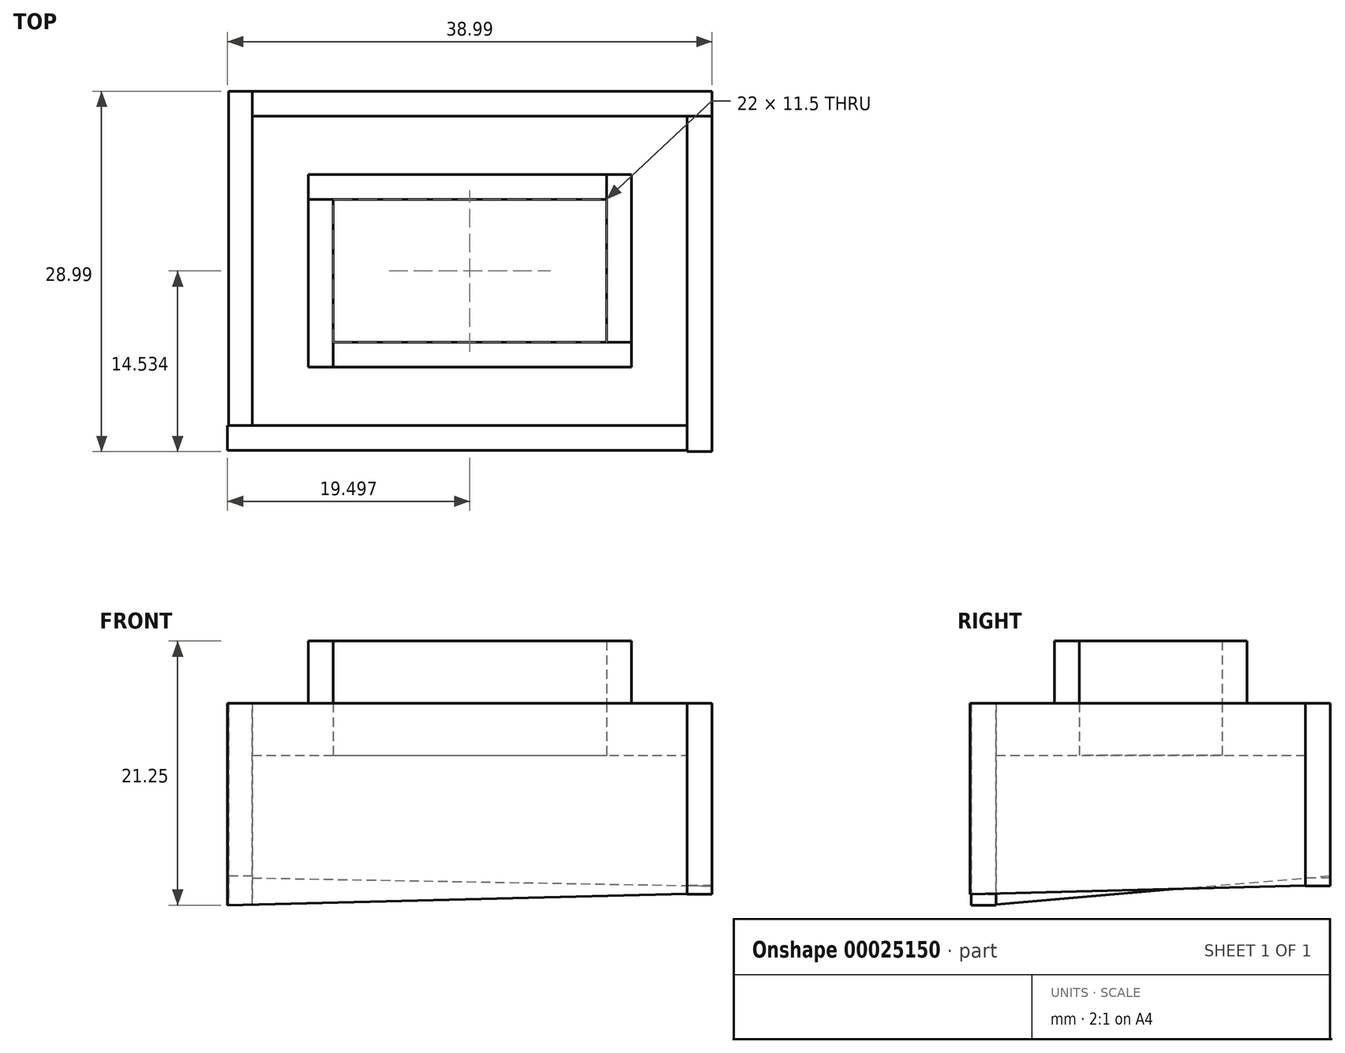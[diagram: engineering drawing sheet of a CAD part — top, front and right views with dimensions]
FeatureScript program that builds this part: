
annotation { "Feature Type Name" : "Feature", "Feature Type Description" : "" }
export const myFeature = defineFeature(function(context is Context, id is Id, definition is map)
    precondition{}
    {
        {
            var Q0;
            Q0=qCreatedBy(makeId("Top.planeOp"),FACE);
            cPlane(context, id + "F0", {"entities" : qUnion([Q0]), "cplaneType" : CPlaneType.OFFSET, "offset" : (12 + 4.2) * mm, "width" : 150 * mm, "height" : 150 * mm});
        }
        {
            var Q0;
            Q0=qCreatedBy(makeId("Right.planeOp"),FACE);
            var sketch = newSketch(context, id + "F1", { "sketchPlane" : qUnion([Q0])});
            skLineSegment(sketch, "E0", {"start": v(0, 0) * mm, "end": v(24.9, 2.14) * mm});
            skLineSegment(sketch, "E1", {"start": v(0, 0) * mm, "end": v(26.9, 2.3) * mm});
            skLineSegment(sketch, "E2", {"start": v(26.9, 2.3) * mm, "end": v(26.9, 16.2) * mm});
            skLineSegment(sketch, "E3", {"start": v(26.9, 16.2) * mm, "end": v(0, 16.2) * mm});
            skLineSegment(sketch, "E4", {"start": v(0, 16.2) * mm, "end": v(0, 0) * mm});
            skLineSegment(sketch, "E5", {"start": v(24.9, 2.14) * mm, "end": v(24.9, 16.2) * mm, "construction": true});
            skSolve(sketch);
        }
        {
            var Q0;
            Q0=qCreatedBy(makeId("Front.planeOp"),FACE);
            var Q1;
            Q1=sQuery(id+"F1.wireOp",VERTEX,"E0.end");
            cPlane(context, id + "F2", {"entities" : qUnion([Q0, Q1]), "cplaneType" : CPlaneType.PLANE_POINT, "offset" : 25 * mm, "width" : 150 * mm, "height" : 150 * mm});
        }
        {
            var Q0;
            Q0=qCreatedBy(id+"F2.planeOp",FACE);
            var sketch = newSketch(context, id + "F3", { "sketchPlane" : qUnion([Q0])});
            skLineSegment(sketch, "E6", {"start": v(0, 2.14) * mm, "end": v(35, 1.52) * mm});
            skLineSegment(sketch, "E7", {"start": v(0, 2.14) * mm, "end": v(37, 1.49) * mm});
            skLineSegment(sketch, "E8", {"start": v(37, 1.49) * mm, "end": v(37, 16.2) * mm});
            skLineSegment(sketch, "E9", {"start": v(37, 16.2) * mm, "end": v(0, 16.2) * mm});
            skLineSegment(sketch, "E10", {"start": v(0, 16.2) * mm, "end": v(0, 2.14) * mm});
            skLineSegment(sketch, "E11", {"start": v(35, 1.52) * mm, "end": v(35, 16.2) * mm, "construction": true});
            skSolve(sketch);
        }
        {
            var Q0;
            Q0=qCreatedBy(makeId("Right.planeOp"),FACE);
            var Q1;
            Q1=sQuery(id+"F3.wireOp",VERTEX,"E6.end");
            cPlane(context, id + "F4", {"entities" : qUnion([Q0, Q1]), "cplaneType" : CPlaneType.PLANE_POINT, "offset" : 25 * mm, "oppositeDirection" : true, "width" : 150 * mm, "height" : 150 * mm});
        }
        {
            var Q0;
            Q0=qCreatedBy(id+"F4.planeOp",FACE);
            var sketch = newSketch(context, id + "F5", { "sketchPlane" : qUnion([Q0])});
            skLineSegment(sketch, "E12", {"start": v(24.9, 1.52) * mm, "end": v(-0.08, 0.87) * mm});
            skLineSegment(sketch, "E13", {"start": v(24.9, 1.52) * mm, "end": v(-2.08, 0.82) * mm});
            skLineSegment(sketch, "E14", {"start": v(-2.08, 0.82) * mm, "end": v(-2.08, 16.2) * mm});
            skLineSegment(sketch, "E15", {"start": v(-2.08, 16.2) * mm, "end": v(24.9, 16.2) * mm});
            skLineSegment(sketch, "E16", {"start": v(24.9, 16.2) * mm, "end": v(24.9, 1.52) * mm});
            skLineSegment(sketch, "E17", {"start": v(-0.08, 0.87) * mm, "end": v(-0.08, 16.2) * mm, "construction": true});
            skSolve(sketch);
        }
        {
            var Q0;
            Q0=qCreatedBy(makeId("Front.planeOp"),FACE);
            var sketch = newSketch(context, id + "F6", { "sketchPlane" : qUnion([Q0])});
            skLineSegment(sketch, "E18", {"start": v(0, 0) * mm, "end": v(34.99, 0.86) * mm});
            skLineSegment(sketch, "E19", {"start": v(34.99, 0.86) * mm, "end": v(-2, -0.05) * mm});
            skLineSegment(sketch, "E20", {"start": v(-2, -0.05) * mm, "end": v(-2, 16.2) * mm});
            skLineSegment(sketch, "E21", {"start": v(-2, 16.2) * mm, "end": v(34.99, 16.2) * mm});
            skLineSegment(sketch, "E22", {"start": v(34.99, 16.2) * mm, "end": v(34.99, 0.86) * mm});
            skLineSegment(sketch, "E23", {"start": v(0, 0) * mm, "end": v(0, 16.2) * mm, "construction": true});
            skSolve(sketch);
        }
        {
            var Q0;
            Q0 = qSketchRegion(id + "F1", true);
            extrude(context, id + "F7", {"entities" : qUnion([Q0]), "oppositeDirection" : true, "depth" : 1.9 * mm, "offsetDistance" : 25 * mm});
        }
        {
            var Q0;
            Q0 = qSketchRegion(id + "F3", true);
            extrude(context, id + "F8", {"entities" : qUnion([Q0]), "oppositeDirection" : true, "depth" : 2 * mm, "offsetDistance" : 25 * mm});
        }
        {
            var Q0;
            Q0 = qSketchRegion(id + "F5", true);
            extrude(context, id + "F9", {"entities" : qUnion([Q0]), "depth" : 2 * mm, "offsetDistance" : 25 * mm});
        }
        {
            var Q0;
            Q0 = qSketchRegion(id + "F6", true);
            extrude(context, id + "F10", {"entities" : qUnion([Q0]), "depth" : 2 * mm, "offsetDistance" : 25 * mm});
        }
        {
            var Q0;
            Q0=qCreatedBy(id+"F0.planeOp",FACE);
            cPlane(context, id + "F11", {"entities" : qUnion([Q0]), "cplaneType" : CPlaneType.OFFSET, "offset" : 4.2 * mm, "oppositeDirection" : true, "width" : 150 * mm, "height" : 150 * mm});
        }
        {
            var Q0;
            Q0=qCreatedBy(id+"F11.planeOp",FACE);
            var sketch = newSketch(context, id + "F12", { "sketchPlane" : qUnion([Q0])});
            skLineSegment(sketch, "E24.bottom", {"start": v(0, 0) * mm, "end": v(35, 0) * mm});
            skLineSegment(sketch, "E24.top", {"start": v(0, 24.9) * mm, "end": v(35, 24.9) * mm});
            skLineSegment(sketch, "E24.left", {"start": v(0, 0) * mm, "end": v(0, 24.9) * mm});
            skLineSegment(sketch, "E24.right", {"start": v(35, 0) * mm, "end": v(35, 24.9) * mm});
            skLineSegment(sketch, "E25", {"start": v(0, 12.45) * mm, "end": v(35, 12.45) * mm, "construction": true});
            skLineSegment(sketch, "E26", {"start": v(17.5, 24.9) * mm, "end": v(17.5, 0) * mm, "construction": true});
            skLineSegment(sketch, "E27.bottom", {"start": v(4.5, 20.2) * mm, "end": v(30.5, 20.2) * mm, "construction": true});
            skLineSegment(sketch, "E27.top", {"start": v(4.5, 4.7) * mm, "end": v(30.5, 4.7) * mm, "construction": true});
            skLineSegment(sketch, "E27.left", {"start": v(4.5, 20.2) * mm, "end": v(4.5, 4.7) * mm, "construction": true});
            skLineSegment(sketch, "E27.right", {"start": v(30.5, 20.2) * mm, "end": v(30.5, 4.7) * mm, "construction": true});
            skPoint(sketch, "E27.middle", {"position": v(17.5, 12.45) * mm});
            skLineSegment(sketch, "E28.0", {"start": v(6.5, 18.2) * mm, "end": v(28.5, 18.2) * mm});
            skLineSegment(sketch, "E28.1", {"start": v(6.5, 18.2) * mm, "end": v(6.5, 6.7) * mm});
            skLineSegment(sketch, "E28.2", {"start": v(6.5, 6.7) * mm, "end": v(28.5, 6.7) * mm});
            skLineSegment(sketch, "E28.3", {"start": v(28.5, 18.2) * mm, "end": v(28.5, 6.7) * mm});
            skLineSegment(sketch, "E29.bottom", {"start": v(31.5, 21.2) * mm, "end": v(3.5, 21.2) * mm, "construction": true});
            skLineSegment(sketch, "E29.top", {"start": v(31.5, 3.7) * mm, "end": v(3.5, 3.7) * mm, "construction": true});
            skLineSegment(sketch, "E29.left", {"start": v(31.5, 21.2) * mm, "end": v(31.5, 3.7) * mm, "construction": true});
            skLineSegment(sketch, "E29.right", {"start": v(3.5, 21.2) * mm, "end": v(3.5, 3.7) * mm, "construction": true});
            skSolve(sketch);
        }
        {
            var Q0;
            Q0=makeQuery(id+"F12.imprint","IMPRINT",FACE,{"disambiguationData":[TD([[makeQuery(id+"F12.imprint","IMPRINT",EDGE,{"derivedFrom":sQuery(id+"F12.wireOp",EDGE,"E24.bottom")}),1.0]])]});
            extrude(context, id + "F13", {"entities" : qUnion([Q0]), "depth" : 4.2 * mm, "offsetDistance" : 25 * mm});
        }
        {
            var Q0;
            Q0=makeQuery(id+"F13.opExtrude","CAP_FACE",FACE,{"disambiguationData":[OSD([sQuery(id+"F12.wireOp",EDGE,"E24.bottom"),sQuery(id+"F12.wireOp",EDGE,"E24.top"),sQuery(id+"F12.wireOp",EDGE,"E24.left"),sQuery(id+"F12.wireOp",EDGE,"E24.right"),sQuery(id+"F12.wireOp",EDGE,"E28.0"),sQuery(id+"F12.wireOp",EDGE,"E28.1"),sQuery(id+"F12.wireOp",EDGE,"E28.2"),sQuery(id+"F12.wireOp",EDGE,"E28.3")])],"isStart":false});
            var sketch = newSketch(context, id + "F14", { "sketchPlane" : qUnion([Q0])});
            skLineSegment(sketch, "E30.bottom", {"start": v(6.5, 18.2) * mm, "end": v(28.5, 18.2) * mm});
            skLineSegment(sketch, "E30.top", {"start": v(6.5, 6.7) * mm, "end": v(28.5, 6.7) * mm});
            skLineSegment(sketch, "E30.left", {"start": v(6.5, 18.2) * mm, "end": v(6.5, 6.7) * mm});
            skLineSegment(sketch, "E30.right", {"start": v(28.5, 18.2) * mm, "end": v(28.5, 6.7) * mm});
            skLineSegment(sketch, "E31.0", {"start": v(4.5, 20.2) * mm, "end": v(30.5, 20.2) * mm});
            skLineSegment(sketch, "E31.1", {"start": v(4.5, 20.2) * mm, "end": v(4.5, 4.7) * mm});
            skLineSegment(sketch, "E31.2", {"start": v(4.5, 4.7) * mm, "end": v(30.5, 4.7) * mm});
            skLineSegment(sketch, "E31.3", {"start": v(30.5, 20.2) * mm, "end": v(30.5, 4.7) * mm});
            skLineSegment(sketch, "E32", {"start": v(6.5, 6.7) * mm, "end": v(6.5, 4.7) * mm});
            skLineSegment(sketch, "E33", {"start": v(28.5, 6.7) * mm, "end": v(30.5, 6.7) * mm});
            skLineSegment(sketch, "E34", {"start": v(28.5, 18.2) * mm, "end": v(28.5, 20.2) * mm});
            skLineSegment(sketch, "E35", {"start": v(6.5, 18.2) * mm, "end": v(4.5, 18.2) * mm});
            skSolve(sketch);
        }
        {
            var Q0;
            Q0=makeQuery(id+"F14.imprint","IMPRINT",FACE,{"disambiguationData":[TD([[makeQuery(id+"F14.imprint","IMPRINT",EDGE,{"derivedFrom":sQuery(id+"F14.wireOp",EDGE,"E30.left")}),-1.0]])]});
            extrude(context, id + "F15", {"entities" : qUnion([Q0]), "depth" : 5 * mm, "offsetDistance" : 25 * mm});
        }
        {
            var Q0;
            Q0=makeQuery(id+"F14.imprint","IMPRINT",FACE,{"disambiguationData":[TD([[makeQuery(id+"F14.imprint","IMPRINT",EDGE,{"derivedFrom":sQuery(id+"F14.wireOp",EDGE,"E30.bottom")}),1.0]])]});
            extrude(context, id + "F16", {"entities" : qUnion([Q0]), "depth" : 5 * mm, "offsetDistance" : 25 * mm});
        }
        {
            var Q0;
            Q0=makeQuery(id+"F14.imprint","IMPRINT",FACE,{"disambiguationData":[TD([[makeQuery(id+"F14.imprint","IMPRINT",EDGE,{"derivedFrom":sQuery(id+"F14.wireOp",EDGE,"E30.right")}),1.0]])]});
            extrude(context, id + "F17", {"entities" : qUnion([Q0]), "depth" : 5 * mm, "offsetDistance" : 25 * mm});
        }
        {
            var Q0;
            Q0=makeQuery(id+"F14.imprint","IMPRINT",FACE,{"disambiguationData":[TD([[makeQuery(id+"F14.imprint","IMPRINT",EDGE,{"derivedFrom":sQuery(id+"F14.wireOp",EDGE,"E30.top")}),-1.0]])]});
            extrude(context, id + "F18", {"entities" : qUnion([Q0]), "depth" : 5 * mm, "offsetDistance" : 25 * mm});
        }
    });
